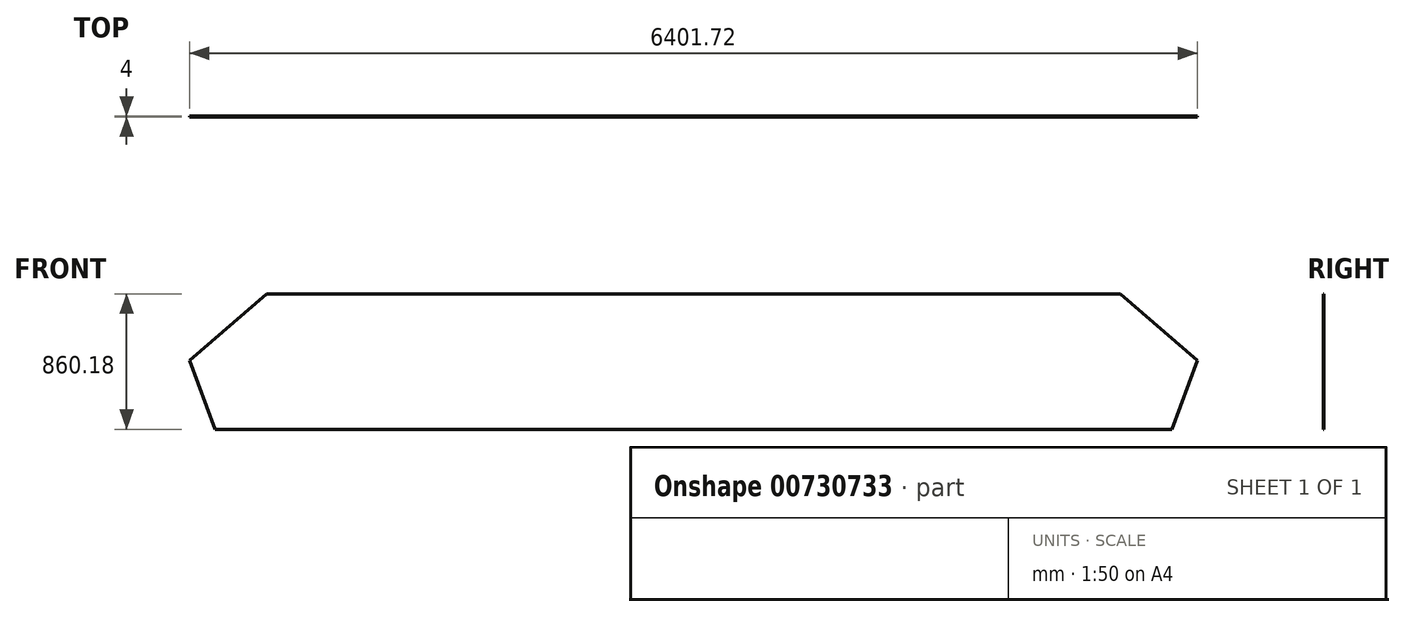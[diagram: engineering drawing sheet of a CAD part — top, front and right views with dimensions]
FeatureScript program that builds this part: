
annotation { "Feature Type Name" : "Feature", "Feature Type Description" : "" }
export const myFeature = defineFeature(function(context is Context, id is Id, definition is map)
    precondition{}
    {
        {
            var Q0;
            Q0=qCreatedBy(makeId("Front.planeOp"),FACE);
            var sketch = newSketch(context, id + "F0", { "sketchPlane" : qUnion([Q0])});
            skLineSegment(sketch, "E0", {"start": v(-3037.92, -430.09) * mm, "end": v(-3200.86, 6.82) * mm});
            skLineSegment(sketch, "E1", {"start": v(-3200.86, 6.82) * mm, "end": v(-2710.43, 430.09) * mm});
            skLineSegment(sketch, "E2", {"start": v(-2710.43, 430.09) * mm, "end": v(0, 430.09) * mm});
            skLineSegment(sketch, "E3", {"start": v(0, 430.09) * mm, "end": v(0, 303.09) * mm});
            skLineSegment(sketch, "E4", {"start": v(0, 303.09) * mm, "end": v(0, 430.09) * mm});
            skLineSegment(sketch, "E5", {"start": v(0, 430.09) * mm, "end": v(2710.43, 430.09) * mm});
            skLineSegment(sketch, "E6", {"start": v(2710.43, 430.09) * mm, "end": v(3200.86, 6.82) * mm});
            skLineSegment(sketch, "E7", {"start": v(3200.86, 6.82) * mm, "end": v(3037.92, -430.09) * mm});
            skLineSegment(sketch, "E8", {"start": v(3037.92, -430.09) * mm, "end": v(0, -430.09) * mm});
            skLineSegment(sketch, "E9", {"start": v(0, -430.09) * mm, "end": v(0, -303.09) * mm});
            skLineSegment(sketch, "E10", {"start": v(0, -303.09) * mm, "end": v(0, -430.09) * mm});
            skLineSegment(sketch, "E11", {"start": v(0, -430.09) * mm, "end": v(-3037.92, -430.09) * mm});
            skSolve(sketch);
        }
        {
            var Q0;
            Q0 = qSketchRegion(id + "F0", true);
            var Q1;
            Q1=makeQuery(id+"F0.imprint","IMPRINT",FACE,{"disambiguationData":[TD([[makeQuery(id+"F0.imprint","IMPRINT",EDGE,{"derivedFrom":sQuery(id+"F0.wireOp",EDGE,"E0")}),-1.0]])]});
            extrude(context, id + "F1", {"entities" : qUnion([Q0, Q1]), "depth" : 4 * mm, "offsetDistance" : 25 * mm});
        }
    });
